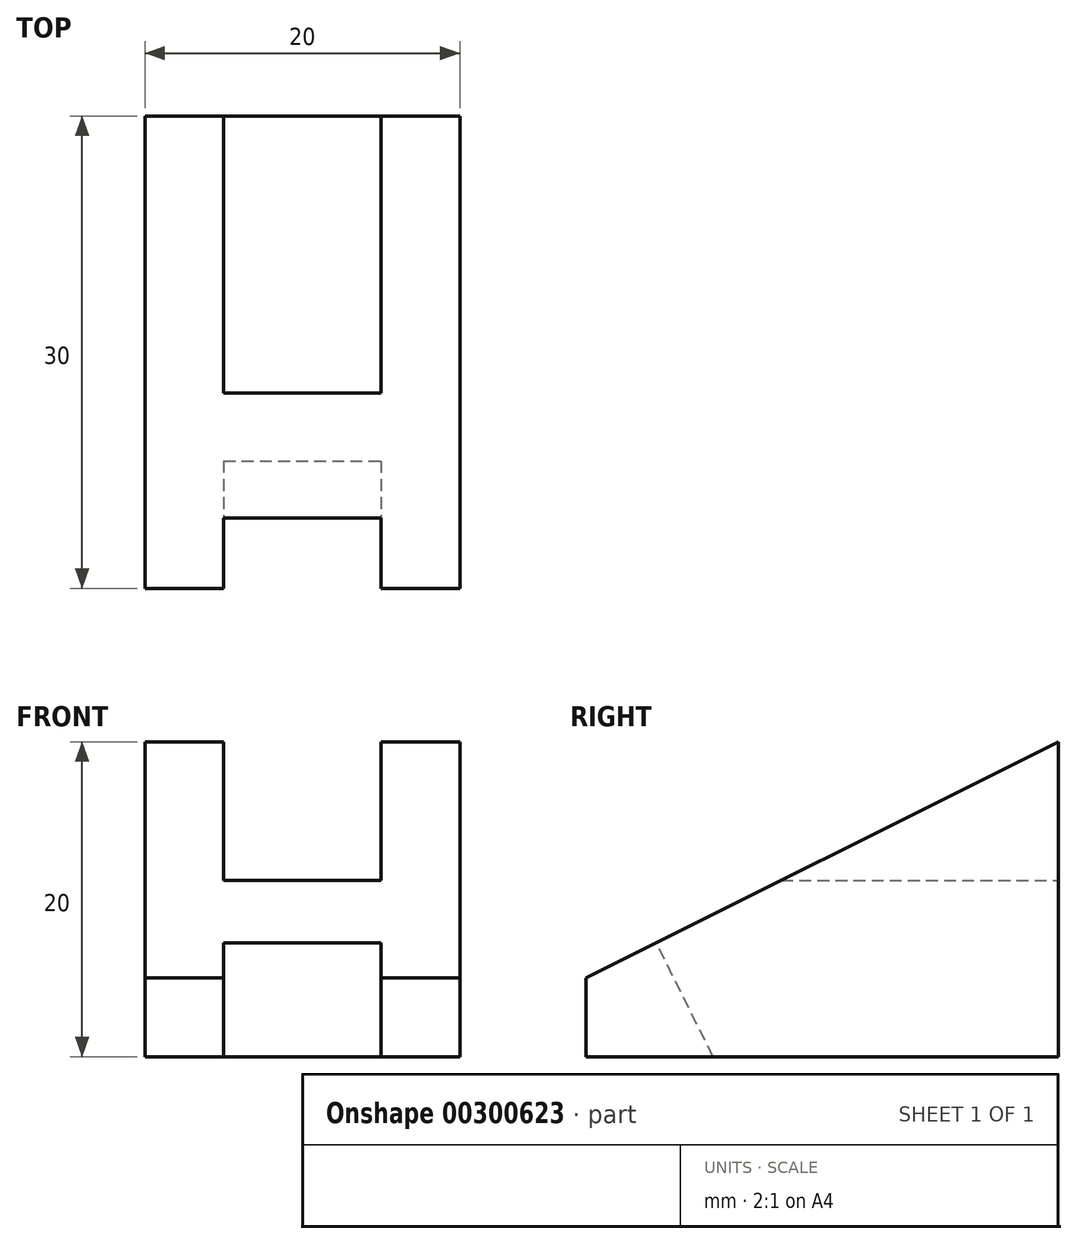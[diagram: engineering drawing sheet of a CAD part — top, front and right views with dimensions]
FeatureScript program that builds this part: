
annotation { "Feature Type Name" : "Feature", "Feature Type Description" : "" }
export const myFeature = defineFeature(function(context is Context, id is Id, definition is map)
    precondition{}
    {
        {
            var Q0;
            Q0=qCreatedBy(makeId("Front.planeOp"),FACE);
            var sketch = newSketch(context, id + "F0", { "sketchPlane" : qUnion([Q0])});
            skLineSegment(sketch, "E0", {"start": v(-10, 0) * mm, "end": v(10, 0) * mm});
            skLineSegment(sketch, "E1", {"start": v(10, 0) * mm, "end": v(10, 20) * mm});
            skLineSegment(sketch, "E2", {"start": v(10, 20) * mm, "end": v(5, 20) * mm});
            skLineSegment(sketch, "E3", {"start": v(5, 20) * mm, "end": v(5, 11.2) * mm});
            skLineSegment(sketch, "E4", {"start": v(5, 11.2) * mm, "end": v(-5, 11.2) * mm});
            skLineSegment(sketch, "E5", {"start": v(-5, 11.2) * mm, "end": v(-5, 20) * mm});
            skLineSegment(sketch, "E6", {"start": v(-5, 20) * mm, "end": v(-10, 20) * mm});
            skLineSegment(sketch, "E7", {"start": v(-10, 20) * mm, "end": v(-10, 0) * mm});
            skSolve(sketch);
        }
        {
            var Q0;
            Q0=makeQuery(id+"F0.imprint","IMPRINT",FACE,{"disambiguationData":[TD([[makeQuery(id+"F0.imprint","IMPRINT",EDGE,{"derivedFrom":sQuery(id+"F0.wireOp",EDGE,"E0")}),1.0]])]});
            extrude(context, id + "F1", {"entities" : qUnion([Q0]), "depth" : 30 * mm});
        }
        {
            var Q0;
            Q0=makeQuery(id+"F1.opExtrude","SWEPT_FACE",FACE,{"disambiguationData":[OSD([sQuery(id+"F0.wireOp",EDGE,"E7")])]});
            var sketch = newSketch(context, id + "F2", { "sketchPlane" : qUnion([Q0])});
            skLineSegment(sketch, "E8", {"start": v(30, 0) * mm, "end": v(30, 5) * mm});
            skLineSegment(sketch, "E9", {"start": v(30, 5) * mm, "end": v(0, 20) * mm});
            skSolve(sketch);
        }
        {
            var Q0;
            {var subQ0=sQuery(id+"F2.wireOp",EDGE,"E9");Q0=makeQuery(id+"F2.imprint","IMPRINT",FACE,{"disambiguationData":[TD([[makeQuery(id+"F2.imprint","IMPRINT",EDGE,{"derivedFrom":subQ0}),-1.0]])]});}
            extrude(context, id + "F3", {"entities" : qUnion([Q0]), "operationType" : NewBodyOperationType.REMOVE, "endBound" : BoundingType.THROUGH_ALL, "oppositeDirection" : true, "depth" : 25 * mm});
        }
        {
            var Q0;
            Q0=makeQuery(id+"F1.opExtrude","CAP_FACE",FACE,{"disambiguationData":[OSD([sQuery(id+"F0.wireOp",EDGE,"E0"),sQuery(id+"F0.wireOp",EDGE,"E1"),sQuery(id+"F0.wireOp",EDGE,"E2"),sQuery(id+"F0.wireOp",EDGE,"E3"),sQuery(id+"F0.wireOp",EDGE,"E4"),sQuery(id+"F0.wireOp",EDGE,"E5"),sQuery(id+"F0.wireOp",EDGE,"E6"),sQuery(id+"F0.wireOp",EDGE,"E7")])],"isStart":false});
            var sketch = newSketch(context, id + "F4", { "sketchPlane" : qUnion([Q0])});
            skLineSegment(sketch, "E10.top", {"start": v(-5, 0) * mm, "end": v(5, 0) * mm});
            skLineSegment(sketch, "E10.left", {"start": v(-5, 5) * mm, "end": v(-5, 0) * mm});
            skLineSegment(sketch, "E10.right", {"start": v(5, 5) * mm, "end": v(5, 0) * mm});
            skLineSegment(sketch, "E11", {"start": v(-5, 2.5) * mm, "end": v(-10, 2.5) * mm});
            skLineSegment(sketch, "E12", {"start": v(5, 2.5) * mm, "end": v(10, 2.5) * mm});
            skLineSegment(sketch, "E13", {"start": v(-5, 5) * mm, "end": v(-5, 10) * mm});
            skLineSegment(sketch, "E14", {"start": v(-5, 10) * mm, "end": v(5, 10) * mm});
            skLineSegment(sketch, "E15", {"start": v(5, 10) * mm, "end": v(5, 5) * mm});
            skSolve(sketch);
        }
        {
            var Q0;
            {var subQ6=sQuery(id+"F4.wireOp",EDGE,"E10.top");Q0=makeQuery(id+"F4.imprint","IMPRINT",FACE,{"disambiguationData":[TD([[makeQuery(id+"F4.imprint","IMPRINT",EDGE,{"derivedFrom":subQ6}),1.0]])]});}
            extrude(context, id + "F5", {"entities" : qUnion([Q0]), "operationType" : NewBodyOperationType.REMOVE, "oppositeDirection" : true, "depth" : 5 * mm});
        }
        {
            var Q0;
            Q0=makeQuery(id+"F3.boolean.opBoolean","COPY",FACE,{"derivedFrom":makeQuery(id+"F3.opExtrude","SWEPT_FACE",FACE,{"disambiguationData":[OSD([sQuery(id+"F2.wireOp",EDGE,"E9")])]})});
            var sketch = newSketch(context, id + "F6", { "sketchPlane" : qUnion([Q0])});
            skLineSegment(sketch, "E16", {"start": v(-5, -24.6) * mm, "end": v(-5, -19.6) * mm});
            skLineSegment(sketch, "E17", {"start": v(-5, -19.6) * mm, "end": v(5, -19.6) * mm});
            skLineSegment(sketch, "E18", {"start": v(5, -19.6) * mm, "end": v(5, -24.6) * mm});
            skSolve(sketch);
        }
        {
            var Q0;
            Q0=makeQuery(id+"F6.imprint","IMPRINT",FACE,{"disambiguationData":[TD([[makeQuery(id+"F6.imprint","IMPRINT",EDGE,{"derivedFrom":sQuery(id+"F6.wireOp",EDGE,"E16")}),-1.0]])]});
            extrude(context, id + "F7", {"entities" : qUnion([Q0]), "operationType" : NewBodyOperationType.REMOVE, "endBound" : BoundingType.THROUGH_ALL, "oppositeDirection" : true, "depth" : 25 * mm});
        }
    });
